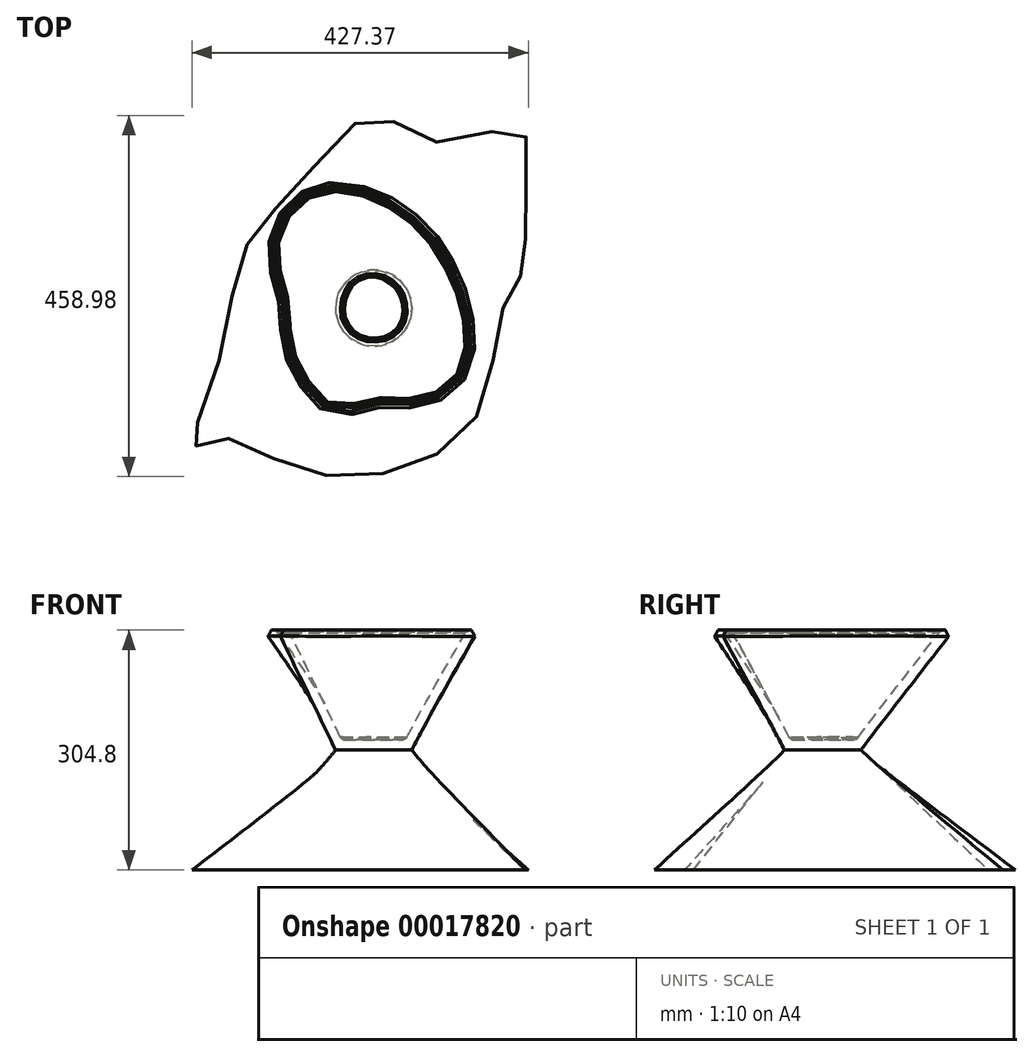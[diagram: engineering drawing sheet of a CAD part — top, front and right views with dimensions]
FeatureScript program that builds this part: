
annotation { "Feature Type Name" : "Feature", "Feature Type Description" : "" }
export const myFeature = defineFeature(function(context is Context, id is Id, definition is map)
    precondition{}
    {
        {
            var Q0;
            Q0=qCreatedBy(makeId("Top.planeOp"),FACE);
            cPlane(context, id + "F0", {"entities" : qUnion([Q0]), "cplaneType" : CPlaneType.OFFSET, "offset" : 152.4 * mm, "width" : 152.4 * mm, "height" : 152.4 * mm});
        }
        {
            var Q0;
            Q0=qCreatedBy(id+"F0.planeOp",FACE);
            var sketch = newSketch(context, id + "F1", { "sketchPlane" : qUnion([Q0])});
            skFitSpline(sketch, "E0", {"points": [v(-123.37, 0) * mm, v(-118.7, -55.32) * mm, v(-55.82, -140.64) * mm, v(0, -131.17) * mm, v(61.33, -130.17) * mm, v(126.69, -80.26) * mm, v(99.6, 69.33) * mm, v(0, 155.86) * mm, v(-94.33, 155.54) * mm, v(-139.74, 77.5) * mm, v(-123.37, 0) * mm]});
            skSolve(sketch);
        }
        {
            var Q0;
            Q0=qCreatedBy(makeId("Top.planeOp"),FACE);
            var sketch = newSketch(context, id + "F2", { "sketchPlane" : qUnion([Q0])});
            skCircle(sketch, "E1", {"center": v(0, 0) * mm, "radius": 48.42 * mm});
            skSolve(sketch);
        }
        {
            var Q0;
            Q0=makeQuery(id+"F2.imprint","IMPRINT",FACE,{"disambiguationData":[TD([[makeQuery(id+"F2.imprint","IMPRINT",EDGE,{"derivedFrom":sQuery(id+"F2.wireOp",EDGE,"E1")}),1.0]])]});
            var Q1;
            Q1=makeQuery(id+"F1.imprint","IMPRINT",FACE,{"disambiguationData":[TD([[makeQuery(id+"F1.imprint","IMPRINT",EDGE,{"derivedFrom":sQuery(id+"F1.wireOp",EDGE,"E0")}),1.0]])]});
            loft(context, id + "F3", {"sheetProfilesArray" : [{ "sheetProfileEntities" : qUnion([Q0]) }, { "sheetProfileEntities" : qUnion([Q1]) }]});
        }
        {
            var Q0;
            Q0=makeQuery(id+"F3.opLoft","CAP_FACE",FACE,{"disambiguationData":[OSD([makeQuery(id+"F1.imprint","IMPRINT",FACE,{"disambiguationData":[TD([[makeQuery(id+"F1.imprint","IMPRINT",EDGE,{"derivedFrom":sQuery(id+"F1.wireOp",EDGE,"E0")}),1.0]])]})])],"isStart":true});
            shell(context, id + "F4", {"entities" : qUnion([Q0]), "thickness" : 12.7 * mm});
        }
        {
            var Q0;
            Q0=makeQuery(id+"F3.opLoft","CAP_FACE",FACE,{"disambiguationData":[OSD([makeQuery(id+"F2.imprint","IMPRINT",FACE,{"disambiguationData":[TD([[makeQuery(id+"F2.imprint","IMPRINT",EDGE,{"derivedFrom":sQuery(id+"F2.wireOp",EDGE,"E1")}),1.0]])]})])],"isStart":true});
            var sketch = newSketch(context, id + "F5", { "sketchPlane" : qUnion([Q0])});
            skCircle(sketch, "E2", {"center": v(0, 0) * mm, "radius": 48.5 * mm});
            skSolve(sketch);
        }
        {
            var Q0;
            Q0=qCreatedBy(makeId("Top.planeOp"),FACE);
            cPlane(context, id + "F6", {"entities" : qUnion([Q0]), "cplaneType" : CPlaneType.OFFSET, "offset" : 152.4 * mm, "oppositeDirection" : true, "width" : 152.4 * mm, "height" : 152.4 * mm});
        }
        {
            var Q0;
            Q0=qCreatedBy(id+"F6.planeOp",FACE);
            var sketch = newSketch(context, id + "F7", { "sketchPlane" : qUnion([Q0])});
            skFitSpline(sketch, "E3", {"points": [v(164.09, 0) * mm, v(134.04, -131.16) * mm, v(29.98, -205.68) * mm, v(-103.52, -201.49) * mm, v(-198.4, -164.72) * mm, v(-230, -175.33) * mm, v(-198.58, -73.57) * mm, v(-162.2, 78.48) * mm, v(-95.17, 156.78) * mm, v(0, 244.8) * mm, v(79.83, 210.81) * mm, v(186.38, 226.66) * mm, v(191.73, 133.84) * mm, v(190.2, 49.45) * mm, v(164.09, 0) * mm]});
            skSolve(sketch);
        }
        {
            var Q0;
            Q0=makeQuery(id+"F7.imprint","IMPRINT",FACE,{"disambiguationData":[TD([[makeQuery(id+"F7.imprint","IMPRINT",EDGE,{"derivedFrom":sQuery(id+"F7.wireOp",EDGE,"E3")}),-1.0]])]});
            var Q1;
            Q1=makeQuery(id+"F5.imprint","IMPRINT",FACE,{"disambiguationData":[TD([[makeQuery(id+"F5.imprint","IMPRINT",EDGE,{"derivedFrom":makeQuery(id+"F3.opLoft","MID_CAP_EDGE",EDGE,{"disambiguationData":[OSD([sQuery(id+"F2.wireOp",EDGE,"E1")])],"capPos":0.0})}),1.0]])]});
            loft(context, id + "F8", {"sheetProfilesArray" : [{ "sheetProfileEntities" : qUnion([Q0]) }, { "sheetProfileEntities" : qUnion([Q1]) }]});
        }
        {
            var Q0;
            Q0=makeQuery(id+"F3.opLoft","MID_CAP_EDGE",EDGE,{"disambiguationData":[OSD([sQuery(id+"F1.wireOp",EDGE,"E0"),sQuery(id+"F2.wireOp",EDGE,"E1")])],"capPos":1.0});
            chamfer(context, id + "F9", {"entities" : qUnion([Q0]), "width" : 5.08 * mm, "tangentPropagation" : true});
        }
        {
            var Q0;
            Q0=makeQuery(id+"F4.opShell","OFFSET_FACE",FACE,{"disambiguationData":[OSD([sQuery(id+"F1.wireOp",EDGE,"E0"),sQuery(id+"F2.wireOp",EDGE,"E1")])]});
            chamfer(context, id + "F10", {"entities" : qUnion([Q0]), "width" : 5.08 * mm, "tangentPropagation" : true});
        }
        {
            var Q0;
            Q0=makeQuery(id+"F4.opShell","OFFSET_FACE",FACE,{"disambiguationData":[OSD([sQuery(id+"F1.wireOp",EDGE,"E0"),sQuery(id+"F2.wireOp",EDGE,"E1")])]});
            fillet(context, id + "F11", {"entities" : qUnion([Q0]), "radius" : 5.08 * mm, "tangentPropagation" : true, "allowEdgeOverflow" : false});
        }
    });
